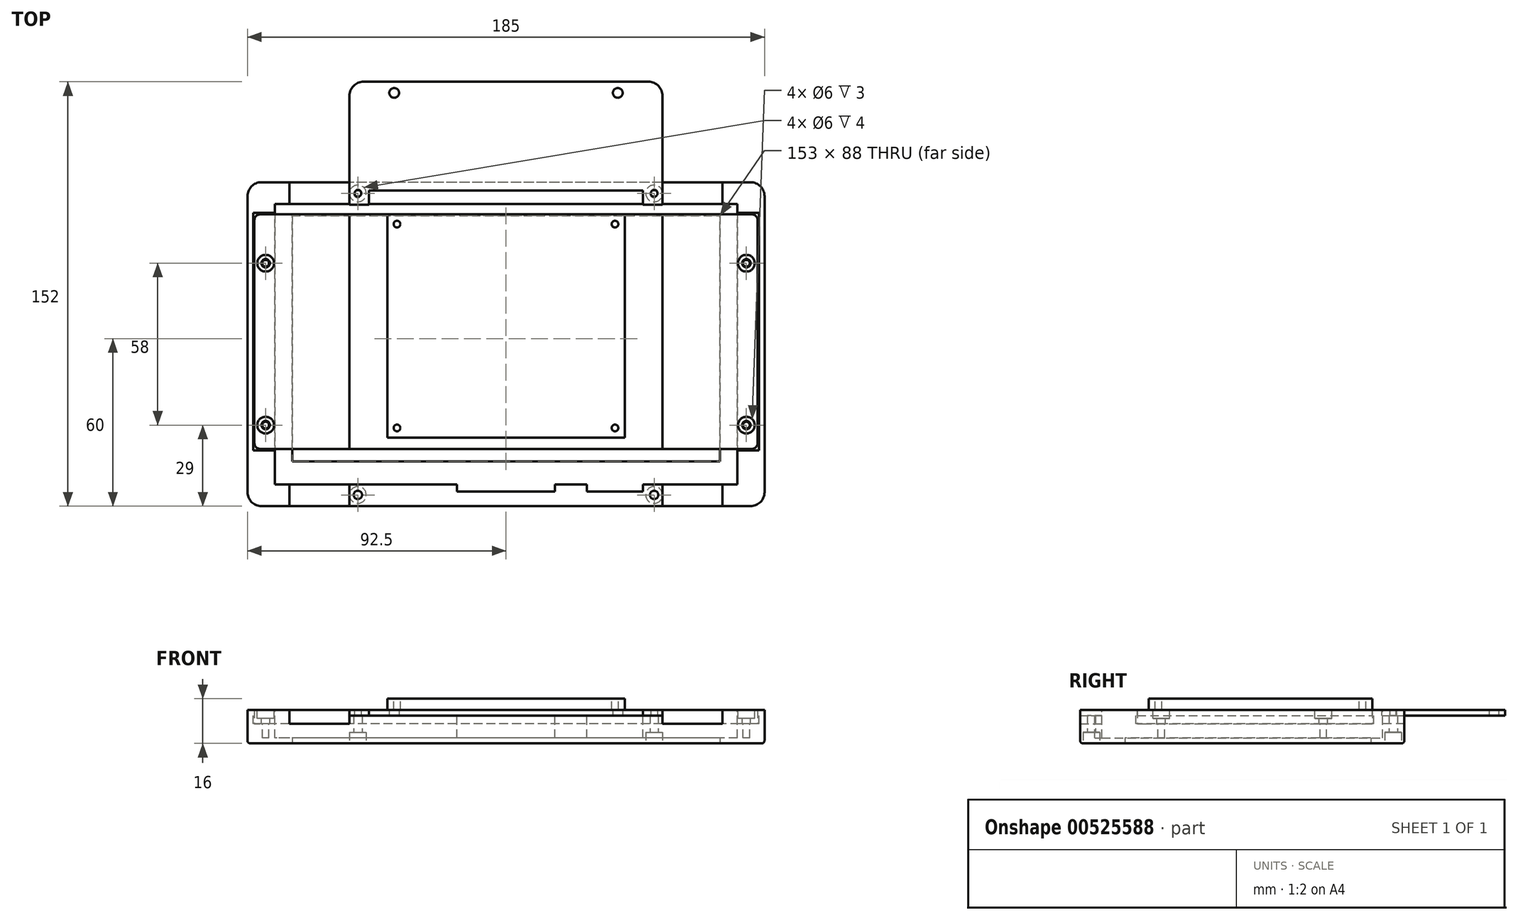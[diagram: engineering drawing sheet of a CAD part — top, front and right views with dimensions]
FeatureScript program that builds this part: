
annotation { "Feature Type Name" : "Feature", "Feature Type Description" : "" }
export const myFeature = defineFeature(function(context is Context, id is Id, definition is map)
    precondition{}
    {
        {
            var Q0;
            Q0=qCreatedBy(makeId("Top.planeOp"),FACE);
            var sketch = newSketch(context, id + "F0", { "sketchPlane" : qUnion([Q0])});
            skLineSegment(sketch, "E0.bottom", {"start": v(82.5, -50) * mm, "end": v(-82.5, -50) * mm, "construction": true});
            skLineSegment(sketch, "E0.top", {"start": v(82.5, 50) * mm, "end": v(-82.5, 50) * mm, "construction": true});
            skLineSegment(sketch, "E0.left", {"start": v(82.5, -50) * mm, "end": v(82.5, 50) * mm, "construction": true});
            skLineSegment(sketch, "E0.right", {"start": v(-82.5, -50) * mm, "end": v(-82.5, 50) * mm, "construction": true});
            skPoint(sketch, "E0.middle", {"position": v(0, 0) * mm});
            skLineSegment(sketch, "E1.bottom", {"start": v(92.5, -58) * mm, "end": v(-92.5, -58) * mm});
            skLineSegment(sketch, "E1.top", {"start": v(92.5, 58) * mm, "end": v(-92.5, 58) * mm});
            skLineSegment(sketch, "E1.left", {"start": v(92.5, -58) * mm, "end": v(92.5, 58) * mm});
            skLineSegment(sketch, "E1.right", {"start": v(-92.5, -58) * mm, "end": v(-92.5, 58) * mm});
            skSolve(sketch);
        }
        {
            var Q0;
            Q0 = qSketchRegion(id + "F0", true);
            extrude(context, id + "F1", {"entities" : qUnion([Q0]), "depth" : 12 * mm, "offsetDistance" : 25 * mm});
        }
        {
            var Q0;
            Q0=makeQuery(id+"F1.opExtrude","CAP_FACE",FACE,{"disambiguationData":[OSD([sQuery(id+"F0.wireOp",EDGE,"E1.bottom"),sQuery(id+"F0.wireOp",EDGE,"E1.top"),sQuery(id+"F0.wireOp",EDGE,"E1.left"),sQuery(id+"F0.wireOp",EDGE,"E1.right")])],"isStart":false});
            var sketch = newSketch(context, id + "F2", { "sketchPlane" : qUnion([Q0])});
            skLineSegment(sketch, "E2.bottom", {"start": v(82.75, -50.25) * mm, "end": v(-82.75, -50.25) * mm});
            skLineSegment(sketch, "E2.top", {"start": v(82.75, 50.25) * mm, "end": v(-82.75, 50.25) * mm});
            skLineSegment(sketch, "E2.left", {"start": v(82.75, -50.25) * mm, "end": v(82.75, 50.25) * mm});
            skLineSegment(sketch, "E2.right", {"start": v(-82.75, -50.25) * mm, "end": v(-82.75, 50.25) * mm});
            skPoint(sketch, "E2.middle", {"position": v(0, 0) * mm});
            skLineSegment(sketch, "E3.bottom", {"start": v(17.5, -52.75) * mm, "end": v(-17.5, -52.75) * mm});
            skLineSegment(sketch, "E3.top", {"start": v(17.5, -50.25) * mm, "end": v(-17.5, -50.25) * mm});
            skLineSegment(sketch, "E3.left", {"start": v(17.5, -52.75) * mm, "end": v(17.5, -50.25) * mm});
            skLineSegment(sketch, "E3.right", {"start": v(-17.5, -52.75) * mm, "end": v(-17.5, -50.25) * mm});
            skPoint(sketch, "E3.middle", {"position": v(0, -51.5) * mm});
            skLineSegment(sketch, "E4.bottom", {"start": v(49, -52.75) * mm, "end": v(29, -52.75) * mm});
            skLineSegment(sketch, "E4.top", {"start": v(49, -50.25) * mm, "end": v(29, -50.25) * mm});
            skLineSegment(sketch, "E4.left", {"start": v(49, -52.75) * mm, "end": v(49, -50.25) * mm});
            skLineSegment(sketch, "E4.right", {"start": v(29, -52.75) * mm, "end": v(29, -50.25) * mm});
            skPoint(sketch, "E4.middle", {"position": v(39, -51.5) * mm});
            skSolve(sketch);
        }
        {
            var Q0;
            Q0 = qSketchRegion(id + "F2", true);
            extrude(context, id + "F3", {"entities" : qUnion([Q0]), "operationType" : NewBodyOperationType.REMOVE, "oppositeDirection" : true, "depth" : 10 * mm, "offsetDistance" : 25 * mm});
        }
        {
            var Q0;
            Q0=makeQuery(id+"F1.opExtrude","CAP_FACE",FACE,{"disambiguationData":[OSD([sQuery(id+"F0.wireOp",EDGE,"E1.bottom"),sQuery(id+"F0.wireOp",EDGE,"E1.top"),sQuery(id+"F0.wireOp",EDGE,"E1.left"),sQuery(id+"F0.wireOp",EDGE,"E1.right")])],"isStart":true});
            var sketch = newSketch(context, id + "F4", { "sketchPlane" : qUnion([Q0])});
            skLineSegment(sketch, "E5.bottom", {"start": v(82.5, -50) * mm, "end": v(-82.5, -50) * mm, "construction": true});
            skLineSegment(sketch, "E5.top", {"start": v(82.5, 50) * mm, "end": v(-82.5, 50) * mm, "construction": true});
            skLineSegment(sketch, "E5.left", {"start": v(82.5, -50) * mm, "end": v(82.5, 50) * mm, "construction": true});
            skLineSegment(sketch, "E5.right", {"start": v(-82.5, -50) * mm, "end": v(-82.5, 50) * mm, "construction": true});
            skPoint(sketch, "E5.middle", {"position": v(0, 0) * mm});
            skLineSegment(sketch, "E6.bottom", {"start": v(-76.5, 42) * mm, "end": v(76.5, 42) * mm});
            skLineSegment(sketch, "E6.top", {"start": v(-76.5, -46) * mm, "end": v(76.5, -46) * mm});
            skLineSegment(sketch, "E6.left", {"start": v(-76.5, 42) * mm, "end": v(-76.5, -46) * mm});
            skLineSegment(sketch, "E6.right", {"start": v(76.5, 42) * mm, "end": v(76.5, -46) * mm});
            skSolve(sketch);
        }
        {
            var Q0;
            Q0 = qSketchRegion(id + "F4", true);
            extrude(context, id + "F5", {"entities" : qUnion([Q0]), "operationType" : NewBodyOperationType.REMOVE, "oppositeDirection" : true, "depth" : 25 * mm, "offsetDistance" : 25 * mm});
        }
        {
            var Q0;
            Q0=makeQuery(id+"F1.opExtrude","CAP_FACE",FACE,{"disambiguationData":[OSD([sQuery(id+"F0.wireOp",EDGE,"E1.bottom"),sQuery(id+"F0.wireOp",EDGE,"E1.top"),sQuery(id+"F0.wireOp",EDGE,"E1.left"),sQuery(id+"F0.wireOp",EDGE,"E1.right")])],"isStart":false});
            var sketch = newSketch(context, id + "F6", { "sketchPlane" : qUnion([Q0])});
            skLineSegment(sketch, "E7.bottom", {"start": v(90.5, -38) * mm, "end": v(-90.5, -38) * mm});
            skLineSegment(sketch, "E7.top", {"start": v(90.5, 47) * mm, "end": v(-90.5, 47) * mm});
            skLineSegment(sketch, "E7.left", {"start": v(90.5, -38) * mm, "end": v(90.5, 47) * mm});
            skLineSegment(sketch, "E7.right", {"start": v(-90.5, -38) * mm, "end": v(-90.5, 47) * mm});
            skPoint(sketch, "E7.middle", {"position": v(0, 4.5) * mm});
            skSolve(sketch);
        }
        {
            var Q0;
            Q0 = qSketchRegion(id + "F6", true);
            extrude(context, id + "F7", {"entities" : qUnion([Q0]), "operationType" : NewBodyOperationType.REMOVE, "oppositeDirection" : true, "depth" : 5 * mm, "offsetDistance" : 25 * mm});
        }
        {
            var Q0;
            {var subQ0=sQuery(id+"F6.wireOp",EDGE,"E7.bottom");var subQ1=sQuery(id+"F6.wireOp",EDGE,"E7.right");var subQ2=sQuery(id+"F6.wireOp",EDGE,"E7.top");Q0=makeQuery(id+"F7.boolean.opBoolean","COPY",FACE,{"disambiguationData":[TD([makeQuery(id+"F3.boolean.opBoolean","COPY",FACE,{"derivedFrom":makeQuery(id+"F3.opExtrude","SWEPT_FACE",FACE,{"disambiguationData":[OSD([sQuery(id+"F2.wireOp",EDGE,"E2.right")])]})})])],"derivedFrom":makeQuery(id+"F7.opExtrude","CAP_FACE",FACE,{"disambiguationData":[OSD([subQ0,subQ2,sQuery(id+"F6.wireOp",EDGE,"E7.left"),subQ1])],"isStart":false})});}
            var sketch = newSketch(context, id + "F8", { "sketchPlane" : qUnion([Q0])});
            skLineSegment(sketch, "E8.bottom", {"start": v(90, -37.5) * mm, "end": v(-90, -37.5) * mm});
            skLineSegment(sketch, "E8.top", {"start": v(90, 46.5) * mm, "end": v(-90, 46.5) * mm});
            skLineSegment(sketch, "E8.left", {"start": v(90, -37.5) * mm, "end": v(90, 46.5) * mm});
            skLineSegment(sketch, "E8.right", {"start": v(-90, -37.5) * mm, "end": v(-90, 46.5) * mm});
            skPoint(sketch, "E8.middle", {"position": v(0, 4.5) * mm});
            skSolve(sketch);
        }
        {
            var Q0;
            Q0 = qSketchRegion(id + "F8", true);
            extrude(context, id + "F9", {"entities" : qUnion([Q0]), "depth" : 5 * mm, "offsetDistance" : 25 * mm});
        }
        {
            var Q0;
            Q0=makeQuery(id+"F1.opExtrude","SWEPT_EDGE",EDGE,{"disambiguationData":[OSD([sQuery(id+"F0.wireOp",EDGE,"E1.top"),sQuery(id+"F0.wireOp",EDGE,"E1.right")])]});
            var Q1;
            Q1=makeQuery(id+"F1.opExtrude","SWEPT_EDGE",EDGE,{"disambiguationData":[OSD([sQuery(id+"F0.wireOp",EDGE,"E1.top"),sQuery(id+"F0.wireOp",EDGE,"E1.left")])]});
            var Q2;
            Q2=makeQuery(id+"F1.opExtrude","SWEPT_EDGE",EDGE,{"disambiguationData":[OSD([sQuery(id+"F0.wireOp",EDGE,"E1.bottom"),sQuery(id+"F0.wireOp",EDGE,"E1.left")])]});
            var Q3;
            Q3=makeQuery(id+"F1.opExtrude","SWEPT_EDGE",EDGE,{"disambiguationData":[OSD([sQuery(id+"F0.wireOp",EDGE,"E1.bottom"),sQuery(id+"F0.wireOp",EDGE,"E1.right")])]});
            fillet(context, id + "F10", {"entities" : qUnion([Q0, Q1, Q2, Q3]), "tangentPropagation" : true, "radius" : 5 * mm, "defaultsChanged" : false, "vertexSettings" : [], "allowEdgeOverflow" : false});
        }
        {
            var Q0;
            Q0=makeQuery(id+"F9.opExtrude","CAP_FACE",FACE,{"disambiguationData":[OSD([sQuery(id+"F8.wireOp",EDGE,"E8.bottom"),sQuery(id+"F8.wireOp",EDGE,"E8.top"),sQuery(id+"F8.wireOp",EDGE,"E8.left"),sQuery(id+"F8.wireOp",EDGE,"E8.right")])],"isStart":false});
            var sketch = newSketch(context, id + "F11", { "sketchPlane" : qUnion([Q0])});
            skCircle(sketch, "E9", {"center": v(-86, 29) * mm, "radius": 1.2 * mm});
            skCircle(sketch, "E10", {"center": v(-86, -29) * mm, "radius": 1.2 * mm});
            skCircle(sketch, "E11.MirrorC", {"center": v(86, -29) * mm, "radius": 1.2 * mm});
            skCircle(sketch, "E12.MirrorC", {"center": v(86, 29) * mm, "radius": 1.2 * mm});
            skSolve(sketch);
        }
        {
            var Q0;
            Q0=sQuery(id+"F11.wireOp",VERTEX,"E9.center");
            var Q1;
            Q1=sQuery(id+"F11.wireOp",VERTEX,"E10.center");
            var Q2;
            Q2=sQuery(id+"F11.wireOp",VERTEX,"E12.MirrorC.center");
            var Q3;
            Q3=sQuery(id+"F11.wireOp",VERTEX,"E11.MirrorC.center");
            var Q4;
            Q4=makeQuery(id+"F9.opExtrude","SWEPT_BODY",BODY,{"disambiguationData":[OSD([sQuery(id+"F8.wireOp",EDGE,"E8.bottom"),sQuery(id+"F8.wireOp",EDGE,"E8.top"),sQuery(id+"F8.wireOp",EDGE,"E8.left"),sQuery(id+"F8.wireOp",EDGE,"E8.right")])]});
            hole(context, id + "F12", {"style" : HoleStyle.C_BORE, "endStyle" : HoleEndStyle.BLIND, "holeDiameter" : 3 * mm, "cBoreDiameter" : 6 * mm, "cBoreDepth" : 3 * mm, "majorDiameter" : 5 * mm, "holeDepth" : 20 * mm, "tappedDepth" : 12 * mm, "tapClearance" : 3, "locations" : qUnion([Q0, Q1, Q2, Q3]), "scope" : qUnion([Q4])});
        }
        {
            var Q0;
            Q0 = qSketchRegion(id + "F11", true);
            extrude(context, id + "F13", {"entities" : qUnion([Q0]), "operationType" : NewBodyOperationType.REMOVE, "oppositeDirection" : true, "depth" : 10 * mm, "offsetDistance" : 25 * mm});
        }
        {
            var Q0;
            Q0=qCreatedBy(makeId("Top.planeOp"),FACE);
            var sketch = newSketch(context, id + "F14", { "sketchPlane" : qUnion([Q0])});
            skLineSegment(sketch, "E13.bottom", {"start": v(54.5, -25.5) * mm, "end": v(-35.5, -25.5) * mm});
            skLineSegment(sketch, "E13.top", {"start": v(54.5, 39.5) * mm, "end": v(-35.5, 39.5) * mm});
            skLineSegment(sketch, "E13.left", {"start": v(54.5, -25.5) * mm, "end": v(54.5, 39.5) * mm});
            skLineSegment(sketch, "E13.right", {"start": v(-35.5, -25.5) * mm, "end": v(-35.5, 39.5) * mm});
            skPoint(sketch, "E13.middle", {"position": v(9.5, 7) * mm});
            skLineSegment(sketch, "E14.bottom", {"start": v(14.5, -25.5) * mm, "end": v(-14.5, -25.5) * mm});
            skLineSegment(sketch, "E14.top", {"start": v(14.5, -20.5) * mm, "end": v(-14.5, -20.5) * mm});
            skLineSegment(sketch, "E14.left", {"start": v(14.5, -25.5) * mm, "end": v(14.5, -20.5) * mm});
            skLineSegment(sketch, "E14.right", {"start": v(-14.5, -25.5) * mm, "end": v(-14.5, -20.5) * mm});
            skPoint(sketch, "E14.middle", {"position": v(0, -23) * mm});
            skLineSegment(sketch, "E15.bottom", {"start": v(50, -50) * mm, "end": v(-50, -50) * mm});
            skLineSegment(sketch, "E15.top", {"start": v(50, 50) * mm, "end": v(-50, 50) * mm});
            skLineSegment(sketch, "E15.left", {"start": v(50, -50) * mm, "end": v(50, 50) * mm});
            skLineSegment(sketch, "E15.right", {"start": v(-50, -50) * mm, "end": v(-50, 50) * mm});
            skPoint(sketch, "E15.middle", {"position": v(0, 0) * mm});
            skCircle(sketch, "E16", {"center": v(-66.5, 52) * mm, "radius": 2.5 * mm, "construction": true});
            skCircle(sketch, "E17.MirrorC", {"center": v(-66.5, -52) * mm, "radius": 2.5 * mm, "construction": true});
            skCircle(sketch, "E18", {"center": v(-66.5, 52) * mm, "radius": 4.5 * mm, "construction": true});
            skSolve(sketch);
        }
        {
            var Q0;
            Q0=makeQuery(id+"F1.opExtrude","CAP_FACE",FACE,{"disambiguationData":[OSD([sQuery(id+"F0.wireOp",EDGE,"E1.bottom"),sQuery(id+"F0.wireOp",EDGE,"E1.top"),sQuery(id+"F0.wireOp",EDGE,"E1.left"),sQuery(id+"F0.wireOp",EDGE,"E1.right")])],"isStart":false});
            var sketch = newSketch(context, id + "F15", { "sketchPlane" : qUnion([Q0])});
            skLineSegment(sketch, "E19.bottom", {"start": v(56, -58) * mm, "end": v(-56, -58) * mm});
            skLineSegment(sketch, "E19.top", {"start": v(56, 58) * mm, "end": v(-56, 58) * mm});
            skLineSegment(sketch, "E19.left", {"start": v(56, -58) * mm, "end": v(56, 58) * mm});
            skLineSegment(sketch, "E19.right", {"start": v(-56, -58) * mm, "end": v(-56, 58) * mm});
            skPoint(sketch, "E19.middle", {"position": v(0, 0) * mm});
            skSolve(sketch);
        }
        {
            var Q0;
            Q0 = qSketchRegion(id + "F15", true);
            extrude(context, id + "F16", {"entities" : qUnion([Q0]), "operationType" : NewBodyOperationType.REMOVE, "oppositeDirection" : true, "depth" : 2 * mm, "offsetDistance" : 25 * mm});
        }
        {
            var Q0;
            Q0=makeQuery(id+"F1.opExtrude","CAP_FACE",FACE,{"disambiguationData":[OSD([sQuery(id+"F0.wireOp",EDGE,"E1.bottom"),sQuery(id+"F0.wireOp",EDGE,"E1.top"),sQuery(id+"F0.wireOp",EDGE,"E1.left"),sQuery(id+"F0.wireOp",EDGE,"E1.right")])],"isStart":true});
            var sketch = newSketch(context, id + "F17", { "sketchPlane" : qUnion([Q0])});
            skPoint(sketch, "E20", {"position": v(-53, 54) * mm});
            skPoint(sketch, "E21", {"position": v(-53, -54) * mm});
            skPoint(sketch, "E22.MirrorP", {"position": v(53, -54) * mm});
            skPoint(sketch, "E23.MirrorP", {"position": v(53, 54) * mm});
            skSolve(sketch);
        }
        {
            var Q0;
            Q0=sQuery(id+"F17.wireOp",VERTEX,"E20");
            var Q1;
            Q1=sQuery(id+"F17.wireOp",VERTEX,"E21");
            var Q2;
            Q2=sQuery(id+"F17.wireOp",VERTEX,"E23.MirrorP");
            var Q3;
            Q3=sQuery(id+"F17.wireOp",VERTEX,"E22.MirrorP");
            var Q4;
            Q4=makeQuery(id+"F1.opExtrude","SWEPT_BODY",BODY,{"disambiguationData":[OSD([sQuery(id+"F0.wireOp",EDGE,"E1.bottom"),sQuery(id+"F0.wireOp",EDGE,"E1.top"),sQuery(id+"F0.wireOp",EDGE,"E1.left"),sQuery(id+"F0.wireOp",EDGE,"E1.right")])]});
            hole(context, id + "F18", {"style" : HoleStyle.C_BORE, "endStyle" : HoleEndStyle.BLIND, "holeDiameter" : 3 * mm, "cBoreDiameter" : 6 * mm, "cBoreDepth" : 4 * mm, "majorDiameter" : 5 * mm, "holeDepth" : 30 * mm, "tappedDepth" : 12 * mm, "tapClearance" : 3, "locations" : qUnion([Q0, Q1, Q2, Q3]), "scope" : qUnion([Q4])});
        }
        {
            var Q0;
            {var subQ0=sQuery(id+"F0.wireOp",EDGE,"E1.right");var subQ1=sQuery(id+"F0.wireOp",EDGE,"E1.bottom");var subQ2=sQuery(id+"F0.wireOp",EDGE,"E1.top");var subQ3=makeQuery(id+"F1.opExtrude","CAP_FACE",FACE,{"disambiguationData":[OSD([subQ1,subQ2,sQuery(id+"F0.wireOp",EDGE,"E1.left"),subQ0])],"isStart":false});Q0=makeQuery(id+"F16.boolean.opBoolean","SPLIT",FACE,{"disambiguationData":[TD([makeQuery(id+"F1.opExtrude","SWEPT_FACE",FACE,{"disambiguationData":[OSD([subQ0])]})])],"derivedFrom":subQ3});}
            var sketch = newSketch(context, id + "F19", { "sketchPlane" : qUnion([Q0])});
            skLineSegment(sketch, "E24.bottom", {"start": v(-56, 58) * mm, "end": v(-77.5, 58) * mm});
            skLineSegment(sketch, "E24.top", {"start": v(-56, 50.25) * mm, "end": v(-77.5, 50.25) * mm});
            skLineSegment(sketch, "E24.left", {"start": v(-56, 58) * mm, "end": v(-56, 50.25) * mm});
            skLineSegment(sketch, "E24.right", {"start": v(-77.5, 58) * mm, "end": v(-77.5, 50.25) * mm});
            skLineSegment(sketch, "E25.MirrorCS", {"start": v(-56, -58) * mm, "end": v(-56, -50.25) * mm});
            skLineSegment(sketch, "E26.MirrorCS", {"start": v(-56, -50.25) * mm, "end": v(-77.5, -50.25) * mm});
            skLineSegment(sketch, "E27.MirrorCS", {"start": v(-77.5, -58) * mm, "end": v(-77.5, -50.25) * mm});
            skLineSegment(sketch, "E28.MirrorCS", {"start": v(-56, -58) * mm, "end": v(-77.5, -58) * mm});
            skLineSegment(sketch, "E29.MirrorCS", {"start": v(56, 58) * mm, "end": v(56, 50.25) * mm});
            skLineSegment(sketch, "E30.MirrorCS", {"start": v(77.5, -58) * mm, "end": v(77.5, -50.25) * mm});
            skLineSegment(sketch, "E31.MirrorCS", {"start": v(56, 58) * mm, "end": v(77.5, 58) * mm});
            skLineSegment(sketch, "E32.MirrorCS", {"start": v(77.5, 58) * mm, "end": v(77.5, 50.25) * mm});
            skLineSegment(sketch, "E33.MirrorCS", {"start": v(56, -50.25) * mm, "end": v(77.5, -50.25) * mm});
            skLineSegment(sketch, "E34.MirrorCS", {"start": v(56, -58) * mm, "end": v(77.5, -58) * mm});
            skLineSegment(sketch, "E35.MirrorCS", {"start": v(56, 50.25) * mm, "end": v(77.5, 50.25) * mm});
            skLineSegment(sketch, "E36.MirrorCS", {"start": v(56, -58) * mm, "end": v(56, -50.25) * mm});
            skSolve(sketch);
        }
        {
            var Q0;
            Q0 = qSketchRegion(id + "F19", true);
            extrude(context, id + "F20", {"entities" : qUnion([Q0]), "operationType" : NewBodyOperationType.REMOVE, "oppositeDirection" : true, "depth" : 5 * mm, "offsetDistance" : 25 * mm});
        }
        {
            var Q0;
            {var subQ0=sQuery(id+"F15.wireOp",EDGE,"E19.left");var subQ1=sQuery(id+"F15.wireOp",EDGE,"E19.right");Q0=makeQuery(id+"F16.boolean.opBoolean","COPY",FACE,{"disambiguationData":[TD([makeQuery(id+"F1.opExtrude","SWEPT_FACE",FACE,{"disambiguationData":[OSD([sQuery(id+"F0.wireOp",EDGE,"E1.top")])]})])],"derivedFrom":makeQuery(id+"F16.opExtrude","CAP_FACE",FACE,{"disambiguationData":[OSD([sQuery(id+"F15.wireOp",EDGE,"E19.bottom"),sQuery(id+"F15.wireOp",EDGE,"E19.top"),subQ0,subQ1])],"isStart":false})});}
            var sketch = newSketch(context, id + "F21", { "sketchPlane" : qUnion([Q0])});
            skLineSegment(sketch, "E37.bottom", {"start": v(56, 50) * mm, "end": v(-56, 50) * mm});
            skLineSegment(sketch, "E37.top", {"start": v(56, 94) * mm, "end": v(-56, 94) * mm});
            skLineSegment(sketch, "E37.left", {"start": v(56, 50) * mm, "end": v(56, 94) * mm});
            skLineSegment(sketch, "E37.right", {"start": v(-56, 50) * mm, "end": v(-56, 94) * mm});
            skPoint(sketch, "E37.middle", {"position": v(0, 72) * mm});
            skCircle(sketch, "E38", {"center": v(-40, 90) * mm, "radius": 1.75 * mm});
            skCircle(sketch, "E39", {"center": v(-53, 54) * mm, "radius": 1.2 * mm});
            skCircle(sketch, "E40.MirrorC", {"center": v(40, 90) * mm, "radius": 1.75 * mm});
            skCircle(sketch, "E41.MirrorC", {"center": v(53, 54) * mm, "radius": 1.2 * mm});
            skSolve(sketch);
        }
        {
            var Q0;
            Q0 = qSketchRegion(id + "F21", true);
            extrude(context, id + "F22", {"entities" : qUnion([Q0]), "depth" : 2 * mm, "offsetDistance" : 25 * mm});
        }
        {
            var Q0;
            Q0=makeQuery(id+"F22.opExtrude","SWEPT_EDGE",EDGE,{"disambiguationData":[OSD([sQuery(id+"F21.wireOp",EDGE,"E37.top"),sQuery(id+"F21.wireOp",EDGE,"E37.right")])]});
            var Q1;
            Q1=makeQuery(id+"F22.opExtrude","SWEPT_EDGE",EDGE,{"disambiguationData":[OSD([sQuery(id+"F21.wireOp",EDGE,"E37.top"),sQuery(id+"F21.wireOp",EDGE,"E37.left")])]});
            fillet(context, id + "F23", {"entities" : qUnion([Q0, Q1]), "tangentPropagation" : true, "radius" : 5 * mm, "defaultsChanged" : false, "vertexSettings" : [], "allowEdgeOverflow" : false});
        }
        {
            var Q0;
            Q0=makeQuery(id+"F9.opExtrude","CAP_FACE",FACE,{"disambiguationData":[OSD([sQuery(id+"F8.wireOp",EDGE,"E8.bottom"),sQuery(id+"F8.wireOp",EDGE,"E8.top"),sQuery(id+"F8.wireOp",EDGE,"E8.left"),sQuery(id+"F8.wireOp",EDGE,"E8.right")])],"isStart":false});
            var sketch = newSketch(context, id + "F24", { "sketchPlane" : qUnion([Q0])});
            skLineSegment(sketch, "E42.bottom", {"start": v(42.5, -33.5) * mm, "end": v(-42.5, -33.5) * mm});
            skLineSegment(sketch, "E42.top", {"start": v(42.5, 46.5) * mm, "end": v(-42.5, 46.5) * mm});
            skLineSegment(sketch, "E42.left", {"start": v(42.5, -33.5) * mm, "end": v(42.5, 46.5) * mm});
            skLineSegment(sketch, "E42.right", {"start": v(-42.5, -33.5) * mm, "end": v(-42.5, 46.5) * mm});
            skPoint(sketch, "E42.middle", {"position": v(0, 6.5) * mm});
            skSolve(sketch);
        }
        {
            var Q0;
            Q0 = qSketchRegion(id + "F24", true);
            extrude(context, id + "F25", {"entities" : qUnion([Q0]), "operationType" : NewBodyOperationType.ADD, "depth" : 4 * mm, "offsetDistance" : 25 * mm});
        }
        {
            var Q0;
            Q0=makeQuery(id+"F25.opExtrude","CAP_FACE",FACE,{"disambiguationData":[OSD([sQuery(id+"F24.wireOp",EDGE,"E42.bottom"),sQuery(id+"F24.wireOp",EDGE,"E42.top"),sQuery(id+"F24.wireOp",EDGE,"E42.left"),sQuery(id+"F24.wireOp",EDGE,"E42.right")])],"isStart":false});
            var sketch = newSketch(context, id + "F26", { "sketchPlane" : qUnion([Q0])});
            skCircle(sketch, "E43", {"center": v(-39, 43) * mm, "radius": 1.2 * mm});
            skCircle(sketch, "E44", {"center": v(39, 43) * mm, "radius": 1.2 * mm});
            skLineSegment(sketch, "E45", {"start": v(-42.5, 6.5) * mm, "end": v(-8.3, 6.5) * mm, "construction": true});
            skCircle(sketch, "E46.MirrorC", {"center": v(-39, -30) * mm, "radius": 1.2 * mm});
            skCircle(sketch, "E47.MirrorC", {"center": v(39, -30) * mm, "radius": 1.2 * mm});
            skSolve(sketch);
        }
        {
            var Q0;
            Q0 = qSketchRegion(id + "F26", true);
            extrude(context, id + "F27", {"entities" : qUnion([Q0]), "operationType" : NewBodyOperationType.REMOVE, "oppositeDirection" : true, "depth" : 6 * mm, "offsetDistance" : 25 * mm});
        }
        {
            var Q0;
            Q0=makeQuery(id+"F9.opExtrude","SWEPT_EDGE",EDGE,{"disambiguationData":[OSD([sQuery(id+"F8.wireOp",EDGE,"E8.top"),sQuery(id+"F8.wireOp",EDGE,"E8.right")])]});
            var Q1;
            Q1=makeQuery(id+"F9.opExtrude","SWEPT_EDGE",EDGE,{"disambiguationData":[OSD([sQuery(id+"F8.wireOp",EDGE,"E8.bottom"),sQuery(id+"F8.wireOp",EDGE,"E8.right")])]});
            var Q2;
            Q2=makeQuery(id+"F9.opExtrude","SWEPT_EDGE",EDGE,{"disambiguationData":[OSD([sQuery(id+"F8.wireOp",EDGE,"E8.bottom"),sQuery(id+"F8.wireOp",EDGE,"E8.left")])]});
            var Q3;
            Q3=makeQuery(id+"F9.opExtrude","SWEPT_EDGE",EDGE,{"disambiguationData":[OSD([sQuery(id+"F8.wireOp",EDGE,"E8.top"),sQuery(id+"F8.wireOp",EDGE,"E8.left")])]});
            fillet(context, id + "F28", {"entities" : qUnion([Q0, Q1, Q2, Q3]), "tangentPropagation" : true, "radius" : 2 * mm, "defaultsChanged" : false, "vertexSettings" : [], "allowEdgeOverflow" : false});
        }
        {
            var Q0;
            Q0=makeQuery(id+"F22.opExtrude","CAP_FACE",FACE,{"disambiguationData":[OSD([sQuery(id+"F21.wireOp",EDGE,"E37.bottom"),sQuery(id+"F21.wireOp",EDGE,"E37.top"),sQuery(id+"F21.wireOp",EDGE,"E37.left"),sQuery(id+"F21.wireOp",EDGE,"E37.right"),sQuery(id+"F21.wireOp",EDGE,"E38"),sQuery(id+"F21.wireOp",EDGE,"E39"),sQuery(id+"F21.wireOp",EDGE,"E40.MirrorC"),sQuery(id+"F21.wireOp",EDGE,"E41.MirrorC")])],"isStart":false});
            var sketch = newSketch(context, id + "F29", { "sketchPlane" : qUnion([Q0])});
            skLineSegment(sketch, "E48.bottom", {"start": v(49, 50) * mm, "end": v(-49, 50) * mm});
            skLineSegment(sketch, "E48.top", {"start": v(49, 55) * mm, "end": v(-49, 55) * mm});
            skLineSegment(sketch, "E48.left", {"start": v(49, 50) * mm, "end": v(49, 55) * mm});
            skLineSegment(sketch, "E48.right", {"start": v(-49, 50) * mm, "end": v(-49, 55) * mm});
            skPoint(sketch, "E48.middle", {"position": v(0, 52.5) * mm});
            skSolve(sketch);
        }
        {
            var Q0;
            Q0 = qSketchRegion(id + "F29", true);
            extrude(context, id + "F30", {"entities" : qUnion([Q0]), "operationType" : NewBodyOperationType.REMOVE, "oppositeDirection" : true, "depth" : 2 * mm, "offsetDistance" : 25 * mm});
        }
        {
            var Q0;
            Q0=makeQuery(id+"F1.opExtrude","CAP_EDGE",EDGE,{"disambiguationData":[OSD([sQuery(id+"F0.wireOp",EDGE,"E1.bottom")])],"isStart":true});
            fillet(context, id + "F31", {"entities" : qUnion([Q0]), "tangentPropagation" : true, "radius" : 1 * mm, "defaultsChanged" : false, "vertexSettings" : [], "allowEdgeOverflow" : false});
        }
    });
